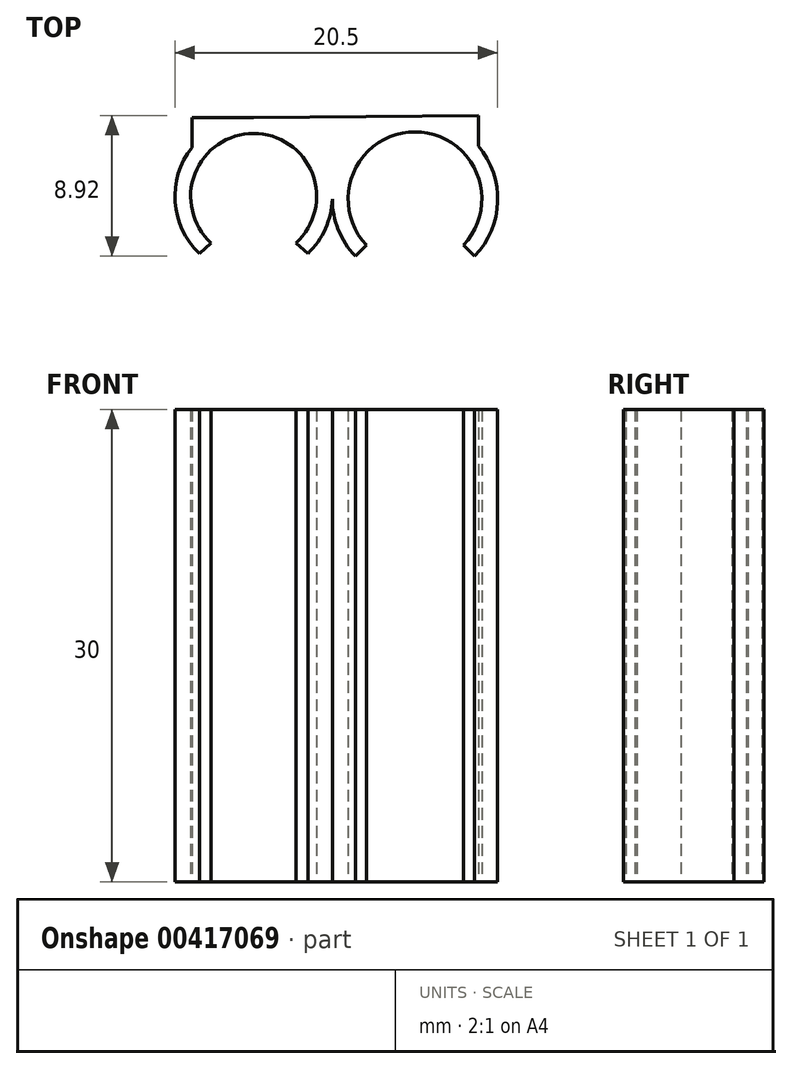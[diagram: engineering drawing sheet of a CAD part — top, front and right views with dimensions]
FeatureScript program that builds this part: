
annotation { "Feature Type Name" : "Feature", "Feature Type Description" : "" }
export const myFeature = defineFeature(function(context is Context, id is Id, definition is map)
    precondition{}
    {
        {
            var Q0;
            Q0=qCreatedBy(makeId("Top.planeOp"),FACE);
            var sketch = newSketch(context, id + "F0", { "sketchPlane" : qUnion([Q0])});
            skArc(sketch, "E0", {"start": v(2.7, -2.95) * mm, "mid": v(0, 4) * mm, "end": v(-2.7, -2.95) * mm});
            skArc(sketch, "E1.0", {"start": v(3.44, -3.63) * mm, "mid": v(0, 5) * mm, "end": v(-3.44, -3.63) * mm});
            skLineSegment(sketch, "E2", {"start": v(-2.7, -2.95) * mm, "end": v(-3.44, -3.63) * mm});
            skLineSegment(sketch, "E3.MirrorCS", {"start": v(2.7, -2.95) * mm, "end": v(3.44, -3.63) * mm});
            skArc(sketch, "E4", {"start": v(14.04, -3.79) * mm, "mid": v(10.25, 5.1) * mm, "end": v(6.46, -3.79) * mm});
            skPoint(sketch, "E4.first.point", {"position": v(5, 0) * mm});
            skPoint(sketch, "E4.second.point", {"position": v(9.27, 5) * mm});
            skPoint(sketch, "E4.third.point", {"position": v(15.5, 0) * mm});
            skArc(sketch, "E5.0", {"start": v(13.33, -3.08) * mm, "mid": v(10.25, 4.1) * mm, "end": v(7.17, -3.08) * mm});
            skLineSegment(sketch, "E6", {"start": v(7.17, -3.08) * mm, "end": v(6.46, -3.79) * mm});
            skLineSegment(sketch, "E7", {"start": v(10.25, -0.16) * mm, "end": v(10.25, -9.33) * mm, "construction": true});
            skLineSegment(sketch, "E8.MirrorCS", {"start": v(13.33, -3.08) * mm, "end": v(14.04, -3.79) * mm});
            skPoint(sketch, "E9.orphan", {"position": v(0, 5) * mm});
            skLineSegment(sketch, "E10", {"start": v(0, 5) * mm, "end": v(10.2, 5.1) * mm});
            skLineSegment(sketch, "E11.0", {"start": v(0, 4) * mm, "end": v(13.3, 4.12) * mm});
            skLineSegment(sketch, "E12", {"start": v(0, 5) * mm, "end": v(-3.92, 5) * mm});
            skLineSegment(sketch, "E13", {"start": v(-3.92, 5) * mm, "end": v(-3.92, 3.1) * mm});
            skLineSegment(sketch, "E14", {"start": v(10.2, 5.1) * mm, "end": v(14.27, 5.13) * mm});
            skLineSegment(sketch, "E15", {"start": v(14.27, 5.13) * mm, "end": v(14.27, 3.21) * mm});
            skSolve(sketch);
        }
        {
            var Q0;
            Q0=qSketchRegion(id+"F0",true);
            var Q1;
            {var subQ0=sQuery(id+"F0.wireOp",EDGE,"E4");var subQ1=sQuery(id+"F0.wireOp",EDGE,"E1.0");var subQ2=makeQuery(id+"F0.imprint","INTERSECT",VERTEX,{"disambiguationData":[OD(1.0)],"derivedFrom":[subQ1,subQ0]});Q1=makeQuery(id+"F0.imprint","IMPRINT",FACE,{"disambiguationData":[TD([[makeQuery(id+"F0.imprint","IMPRINT",EDGE,{"disambiguationData":[TD([[subQ2,-1.0]])],"derivedFrom":subQ1}),-1.0]])]});}
            extrude(context, id + "F1", {"entities" : qUnion([Q0, Q1]), "depth" : 30 * mm, "offsetDistance" : 25 * mm});
        }
        {
            var Q0;
            Q0=makeQuery(id+"F1.opExtrude","SWEPT_EDGE",EDGE,{"disambiguationData":[OSD([sQuery(id+"F0.wireOp",EDGE,"E11.0"),sQuery(id+"F0.wireOp",EDGE,"XwcOn8LO-vP9B-Yd7K-vXvg-Oq0ZhfRHlDl5")])]});
            var Q1;
            Q1=makeQuery(id+"F1.opExtrude","SWEPT_EDGE",EDGE,{"disambiguationData":[OSD([sQuery(id+"F0.wireOp",EDGE,"d9e671d5-69bc-470e-aa7c-eaaee2be7675.0"),sQuery(id+"F0.wireOp",EDGE,"XwcOn8LO-vP9B-Yd7K-vXvg-Oq0ZhfRHlDl5")])]});
            var Q2;
            Q2=makeQuery(id+"F1.opExtrude","SWEPT_EDGE",EDGE,{"disambiguationData":[OSD([sQuery(id+"F0.wireOp",EDGE,"98dbefde-4300-4ddc-83c5-26b99558cf72.0"),sQuery(id+"F0.wireOp",EDGE,"EuGeefs3-axDX-KbgD-0TMg-BFDRTn4chRv0")])]});
            var Q3;
            Q3=makeQuery(id+"F1.opExtrude","SWEPT_EDGE",EDGE,{"disambiguationData":[OSD([sQuery(id+"F0.wireOp",EDGE,"E10"),sQuery(id+"F0.wireOp",EDGE,"EuGeefs3-axDX-KbgD-0TMg-BFDRTn4chRv0")])]});
            var Q4;
            Q4=makeQuery(id+"F1.opExtrude","SWEPT_EDGE",EDGE,{"disambiguationData":[OSD([sQuery(id+"F0.wireOp",EDGE,"c14db151-7bc4-4e69-aadb-7e66df819bd6.0"),sQuery(id+"F0.wireOp",EDGE,"Jny5aJNN-UiSH-fCwR-GJDF-LtWWNU0N78co")])]});
            var Q5;
            Q5=makeQuery(id+"F1.opExtrude","SWEPT_EDGE",EDGE,{"disambiguationData":[OSD([sQuery(id+"F0.wireOp",EDGE,"lQOSFRey-aMqZ-RI4Z-CSTS-nsqwqvjwZoFW"),sQuery(id+"F0.wireOp",EDGE,"Jny5aJNN-UiSH-fCwR-GJDF-LtWWNU0N78co")])]});
            fillet(context, id + "F2", {"entities" : qUnion([Q0, Q1, Q2, Q3, Q4, Q5]), "radius" : 1 * mm, "tangentPropagation" : true, "allowEdgeOverflow" : false});
        }
    });
